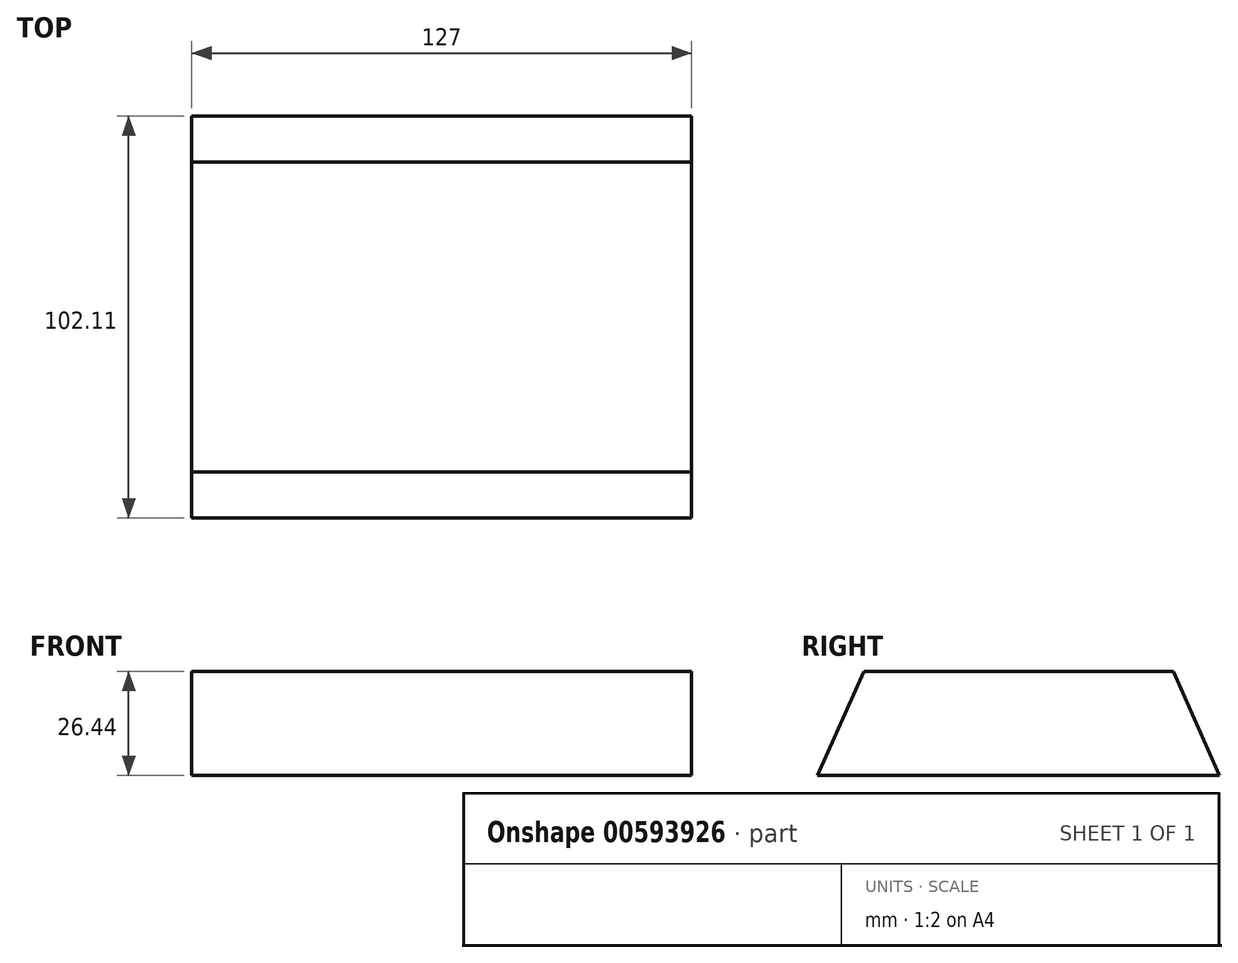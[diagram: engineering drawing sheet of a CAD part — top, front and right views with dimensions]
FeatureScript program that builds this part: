
annotation { "Feature Type Name" : "Feature", "Feature Type Description" : "" }
export const myFeature = defineFeature(function(context is Context, id is Id, definition is map)
    precondition{}
    {
        {
            var Q0;
            Q0=qCreatedBy(makeId("Right.planeOp"),FACE);
            var sketch = newSketch(context, id + "F0", { "sketchPlane" : qUnion([Q0])});
            skLineSegment(sketch, "E0", {"start": v(-44.64, 26.44) * mm, "end": v(34.01, 26.44) * mm});
            skLineSegment(sketch, "E1", {"start": v(34.01, 26.44) * mm, "end": v(45.74, 0) * mm});
            skLineSegment(sketch, "E2", {"start": v(45.74, 0) * mm, "end": v(-56.37, 0) * mm});
            skLineSegment(sketch, "E3", {"start": v(-44.64, 26.44) * mm, "end": v(-56.37, 0) * mm});
            skLineSegment(sketch, "E4", {"start": v(-44.64, 26.44) * mm, "end": v(-39.4, 0) * mm});
            skLineSegment(sketch, "E5", {"start": v(-39.4, 0) * mm, "end": v(-27.67, 26.44) * mm});
            skLineSegment(sketch, "E6", {"start": v(-27.67, 26.44) * mm, "end": v(-22.42, 0) * mm});
            skLineSegment(sketch, "E7", {"start": v(-23.08, 0) * mm, "end": v(-11.35, 26.44) * mm});
            skLineSegment(sketch, "E8", {"start": v(-11.35, 26.44) * mm, "end": v(-6.1, 0) * mm});
            skLineSegment(sketch, "E9", {"start": v(-6.1, 0) * mm, "end": v(5.62, 26.44) * mm});
            skSolve(sketch);
        }
        {
            var Q0;
            Q0 = qSketchRegion(id + "F0", true);
            extrude(context, id + "F1", {"entities" : qUnion([Q0]), "endBound" : BoundingType.SYMMETRIC, "depth" : 127 * mm, "offsetDistance" : 25.4 * mm});
        }
    });
